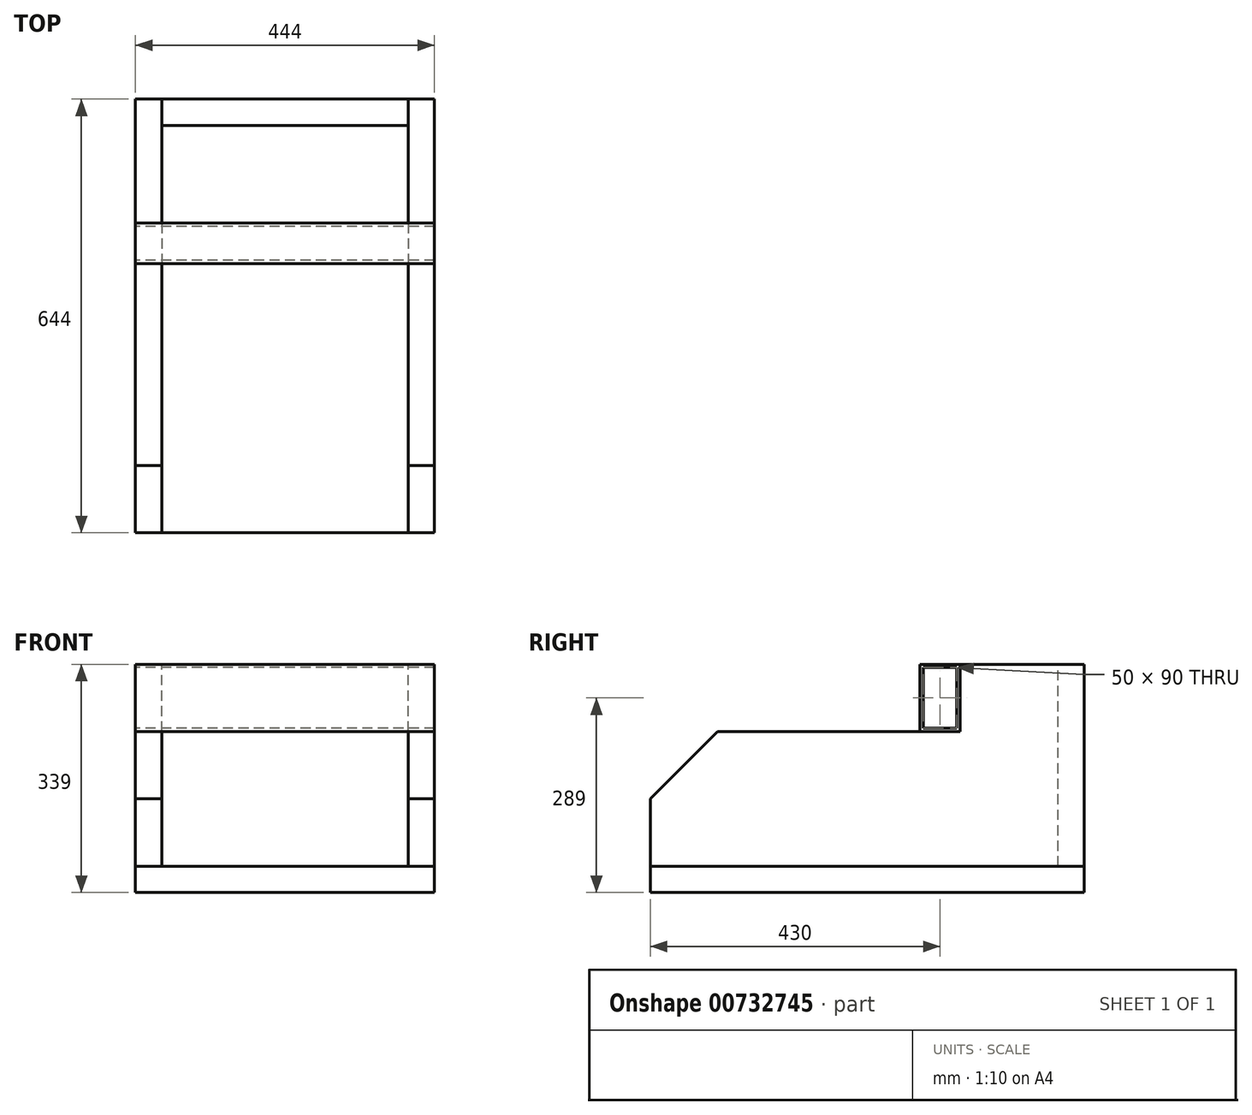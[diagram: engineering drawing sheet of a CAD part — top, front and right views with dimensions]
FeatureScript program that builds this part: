
annotation { "Feature Type Name" : "Feature", "Feature Type Description" : "" }
export const myFeature = defineFeature(function(context is Context, id is Id, definition is map)
    precondition{}
    {
        {
            var Q0;
            Q0=qCreatedBy(makeId("Top.planeOp"),FACE);
            var sketch = newSketch(context, id + "F0", { "sketchPlane" : qUnion([Q0])});
            skLineSegment(sketch, "E0.bottom", {"start": v(222, -322) * mm, "end": v(-222, -322) * mm});
            skLineSegment(sketch, "E0.top", {"start": v(222, 322) * mm, "end": v(-222, 322) * mm});
            skLineSegment(sketch, "E0.left", {"start": v(222, -322) * mm, "end": v(222, 322) * mm});
            skLineSegment(sketch, "E0.right", {"start": v(-222, -322) * mm, "end": v(-222, 322) * mm});
            skPoint(sketch, "E0.middle", {"position": v(0, 0) * mm});
            skSolve(sketch);
        }
        {
            var Q0;
            Q0 = qSketchRegion(id + "F0", true);
            extrude(context, id + "F1", {"entities" : qUnion([Q0]), "depth" : 39 * mm, "offsetDistance" : 25 * mm});
        }
        {
            var Q0;
            Q0=makeQuery(id+"F1.opExtrude","SWEPT_FACE",FACE,{"disambiguationData":[OSD([sQuery(id+"F0.wireOp",EDGE,"E0.bottom")])]});
            var sketch = newSketch(context, id + "F2", { "sketchPlane" : qUnion([Q0])});
            skLineSegment(sketch, "E1.bottom", {"start": v(-222, 39) * mm, "end": v(-183, 39) * mm});
            skLineSegment(sketch, "E1.top", {"start": v(-222, 239) * mm, "end": v(-183, 239) * mm});
            skLineSegment(sketch, "E1.left", {"start": v(-222, 39) * mm, "end": v(-222, 239) * mm});
            skLineSegment(sketch, "E1.right", {"start": v(-183, 39) * mm, "end": v(-183, 239) * mm});
            skSolve(sketch);
        }
        {
            var Q0;
            Q0 = qSketchRegion(id + "F2", true);
            var Q1;
            Q1=makeQuery(id+"F1.opExtrude","SWEPT_FACE",FACE,{"disambiguationData":[OSD([sQuery(id+"F0.wireOp",EDGE,"E0.top")])]});
            extrude(context, id + "F3", {"entities" : qUnion([Q0]), "endBound" : BoundingType.UP_TO_SURFACE, "oppositeDirection" : true, "depth" : 25 * mm, "endBoundEntityFace" : qUnion([Q1]), "offsetDistance" : 25 * mm});
        }
        {
            var Q0;
            Q0=makeQuery(id+"F3.opExtrude","SWEPT_FACE",FACE,{"disambiguationData":[OSD([sQuery(id+"F2.wireOp",EDGE,"E1.left")])]});
            var sketch = newSketch(context, id + "F4", { "sketchPlane" : qUnion([Q0])});
            skLineSegment(sketch, "E2.bottom", {"start": v(-322, 239) * mm, "end": v(-138, 239) * mm});
            skLineSegment(sketch, "E2.top", {"start": v(-322, 339) * mm, "end": v(-138, 339) * mm});
            skLineSegment(sketch, "E2.left", {"start": v(-322, 239) * mm, "end": v(-322, 339) * mm});
            skLineSegment(sketch, "E2.right", {"start": v(-138, 239) * mm, "end": v(-138, 339) * mm});
            skSolve(sketch);
        }
        {
            var Q0;
            Q0 = qSketchRegion(id + "F4", true);
            extrude(context, id + "F5", {"entities" : qUnion([Q0]), "operationType" : NewBodyOperationType.ADD, "oppositeDirection" : true, "depth" : 39 * mm, "offsetDistance" : 25 * mm});
        }
        {
            var Q0;
            Q0=makeQuery(id+"F3.opExtrude","SWEPT_BODY",BODY,{"disambiguationData":[OSD([sQuery(id+"F2.wireOp",EDGE,"E1.bottom"),sQuery(id+"F2.wireOp",EDGE,"E1.top"),sQuery(id+"F2.wireOp",EDGE,"E1.left"),sQuery(id+"F2.wireOp",EDGE,"E1.right")])]});
            var Q1;
            Q1=qCreatedBy(makeId("Right.planeOp"),FACE);
            mirror(context, id + "F6", {"entities" : qUnion([Q0]), "mirrorPlane" : qUnion([Q1])});
        }
        {
            var Q0;
            Q0=makeQuery(id+"F6.opPattern","COPY",FACE,{"derivedFrom":makeQuery(id+"F3.opExtrude","SWEPT_FACE",FACE,{"disambiguationData":[OSD([sQuery(id+"F2.wireOp",EDGE,"E1.right")])]}),"instanceName":"1"});
            var sketch = newSketch(context, id + "F7", { "sketchPlane" : qUnion([Q0])});
            skLineSegment(sketch, "E3.bottom", {"start": v(-322, 339) * mm, "end": v(-283, 339) * mm});
            skLineSegment(sketch, "E3.top", {"start": v(-322, 39) * mm, "end": v(-283, 39) * mm});
            skLineSegment(sketch, "E3.left", {"start": v(-322, 339) * mm, "end": v(-322, 39) * mm});
            skLineSegment(sketch, "E3.right", {"start": v(-283, 339) * mm, "end": v(-283, 39) * mm});
            skSolve(sketch);
        }
        {
            var Q0;
            Q0 = qSketchRegion(id + "F7", true);
            extrude(context, id + "F8", {"entities" : qUnion([Q0]), "endBound" : BoundingType.UP_TO_NEXT, "depth" : 25 * mm, "offsetDistance" : 25 * mm});
        }
        {
            var Q0;
            Q0=makeQuery(id+"F3.opExtrude","CAP_EDGE",EDGE,{"disambiguationData":[OSD([sQuery(id+"F2.wireOp",EDGE,"E1.top")])],"isStart":true});
            var Q1;
            Q1=makeQuery(id+"F6.opPattern","COPY",EDGE,{"derivedFrom":makeQuery(id+"F3.opExtrude","CAP_EDGE",EDGE,{"disambiguationData":[OSD([sQuery(id+"F2.wireOp",EDGE,"E1.top")])],"isStart":true}),"instanceName":"1"});
            chamfer(context, id + "F9", {"entities" : qUnion([Q0, Q1]), "width" : 100 * mm, "tangentPropagation" : true});
        }
        {
            var Q0;
            Q0=makeQuery(id+"F3.opExtrude","SWEPT_FACE",FACE,{"disambiguationData":[OSD([sQuery(id+"F2.wireOp",EDGE,"E1.left")])]});
            var sketch = newSketch(context, id + "F10", { "sketchPlane" : qUnion([Q0])});
            skLineSegment(sketch, "E4.bottom", {"start": v(-78, 239) * mm, "end": v(-138, 239) * mm});
            skLineSegment(sketch, "E4.top", {"start": v(-78, 339) * mm, "end": v(-138, 339) * mm});
            skLineSegment(sketch, "E4.left", {"start": v(-78, 239) * mm, "end": v(-78, 339) * mm});
            skLineSegment(sketch, "E4.right", {"start": v(-138, 239) * mm, "end": v(-138, 339) * mm});
            skLineSegment(sketch, "E5.0", {"start": v(-133, 244) * mm, "end": v(-133, 334) * mm});
            skLineSegment(sketch, "E5.1", {"start": v(-83, 244) * mm, "end": v(-133, 244) * mm});
            skLineSegment(sketch, "E5.2", {"start": v(-83, 244) * mm, "end": v(-83, 334) * mm});
            skLineSegment(sketch, "E5.3", {"start": v(-83, 334) * mm, "end": v(-133, 334) * mm});
            skSolve(sketch);
        }
        {
            var Q0;
            Q0 = qSketchRegion(id + "F10", true);
            var Q1;
            Q1=makeQuery(id+"F6.opPattern","COPY",FACE,{"derivedFrom":makeQuery(id+"F3.opExtrude","SWEPT_FACE",FACE,{"disambiguationData":[OSD([sQuery(id+"F2.wireOp",EDGE,"E1.left")])]}),"instanceName":"1"});
            extrude(context, id + "F11", {"entities" : qUnion([Q0]), "endBound" : BoundingType.UP_TO_SURFACE, "oppositeDirection" : true, "depth" : 450 * mm, "endBoundEntityFace" : qUnion([Q1]), "offsetDistance" : 25 * mm});
        }
    });
